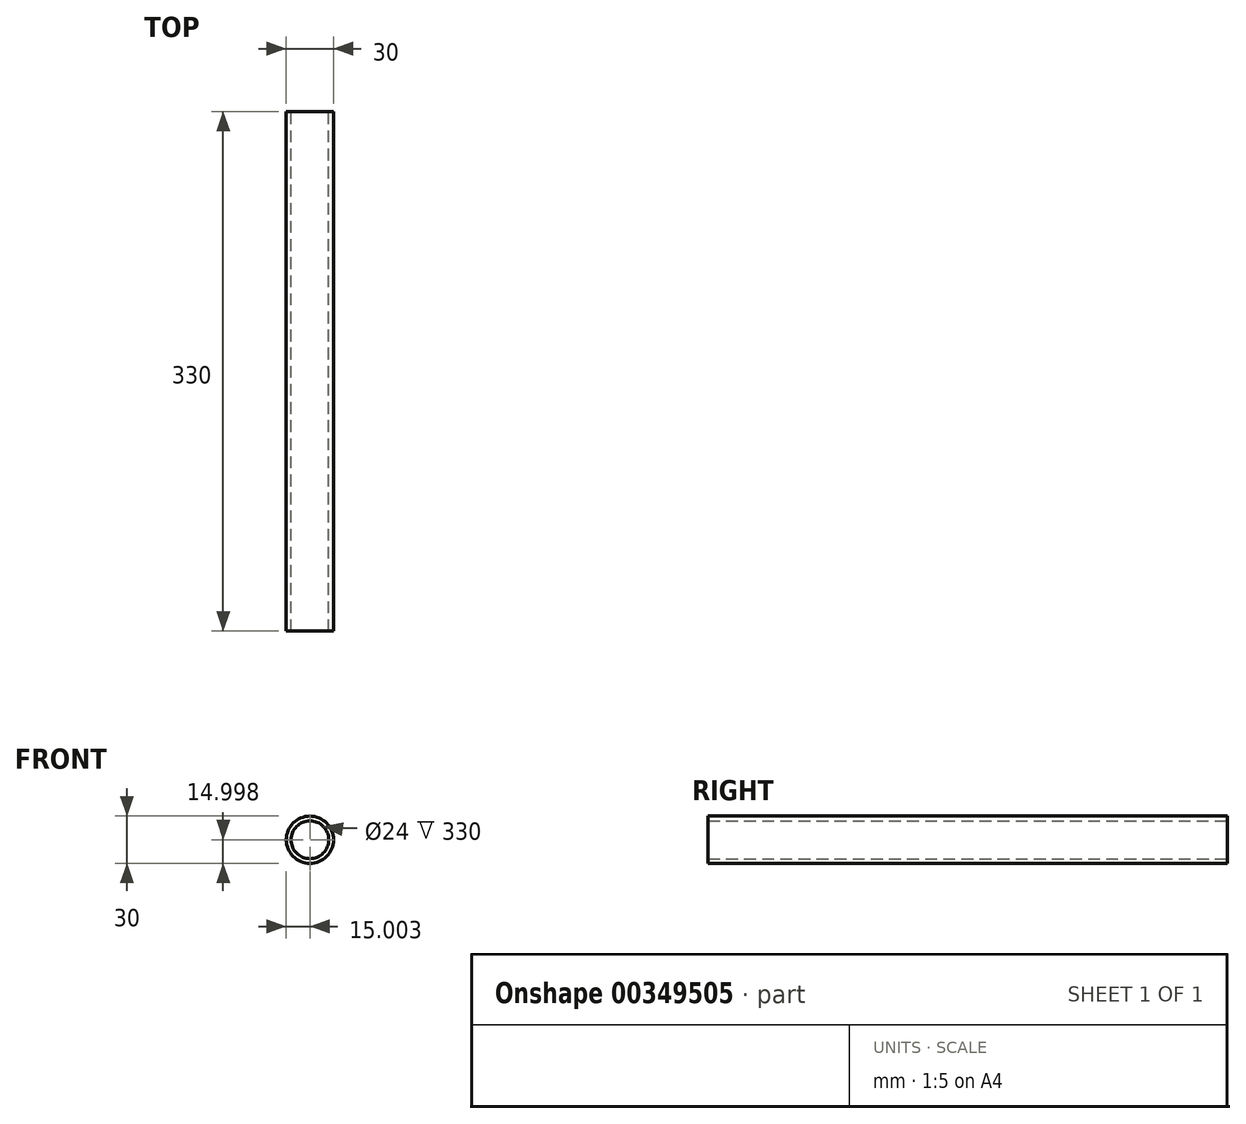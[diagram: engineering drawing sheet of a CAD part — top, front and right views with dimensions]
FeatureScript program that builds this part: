
annotation { "Feature Type Name" : "Feature", "Feature Type Description" : "" }
export const myFeature = defineFeature(function(context is Context, id is Id, definition is map)
    precondition{}
    {
        {
            var Q0;
            Q0=qCreatedBy(makeId("Front.planeOp"),FACE);
            var sketch = newSketch(context, id + "F0", { "sketchPlane" : qUnion([Q0])});
            skCircle(sketch, "E0", {"center": v(-63.3, 20.5) * mm, "radius": 15 * mm});
            skCircle(sketch, "E1.0", {"center": v(-63.3, 20.5) * mm, "radius": 12 * mm});
            skSolve(sketch);
        }
        {
            var Q0;
            Q0 = qSketchRegion(id + "F0", true);
            extrude(context, id + "F1", {"entities" : qUnion([Q0]), "depth" : 330 * mm, "symmetric" : true});
        }
    });
